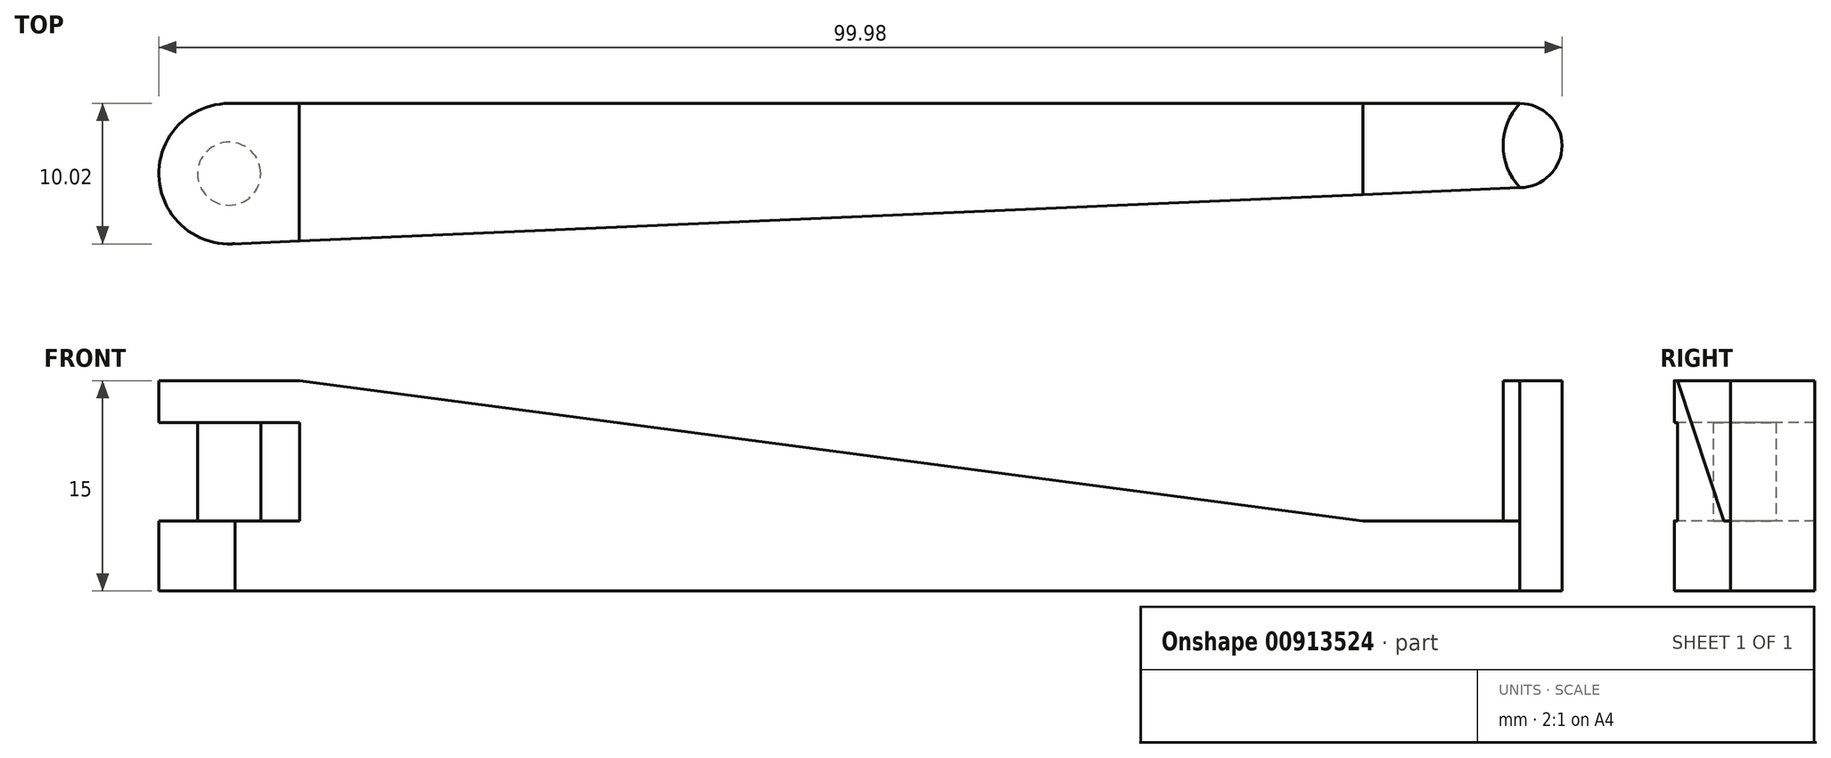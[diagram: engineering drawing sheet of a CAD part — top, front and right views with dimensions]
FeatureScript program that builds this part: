
annotation { "Feature Type Name" : "Feature", "Feature Type Description" : "" }
export const myFeature = defineFeature(function(context is Context, id is Id, definition is map)
    precondition{}
    {
        {
            var Q0;
            Q0=qCreatedBy(makeId("Top.planeOp"),FACE);
            var sketch = newSketch(context, id + "F0", { "sketchPlane" : qUnion([Q0])});
            skArc(sketch, "E0", {"start": v(0, -21.01) * mm, "mid": v(-5, -26.24) * mm, "end": v(0.44, -31.01) * mm});
            skLineSegment(sketch, "E1", {"start": v(0, -21.01) * mm, "end": v(91.97, -21.01) * mm});
            skArc(sketch, "E2", {"start": v(91.97, -27.01) * mm, "mid": v(94.97, -24.01) * mm, "end": v(91.97, -21.01) * mm});
            skLineSegment(sketch, "E3", {"start": v(0, -31.03) * mm, "end": v(91.97, -27.01) * mm});
            skSolve(sketch);
        }
        {
            var Q0;
            Q0 = qSketchRegion(id + "F0", true);
            extrude(context, id + "F1", {"entities" : qUnion([Q0]), "depth" : 5 * mm, "offsetDistance" : 25 * mm});
        }
        {
            var Q0;
            Q0=makeQuery(id+"F1.opExtrude","CAP_FACE",FACE,{"disambiguationData":[OSD([sQuery(id+"F0.wireOp",EDGE,"E0"),sQuery(id+"F0.wireOp",EDGE,"E1"),sQuery(id+"F0.wireOp",EDGE,"E2"),sQuery(id+"F0.wireOp",EDGE,"E3")])],"isStart":false});
            var sketch = newSketch(context, id + "F2", { "sketchPlane" : qUnion([Q0])});
            skArc(sketch, "E4.0", {"start": v(91.97, -27.01) * mm, "mid": v(94.97, -24.01) * mm, "end": v(91.97, -21.01) * mm});
            skPoint(sketch, "E4.1", {"position": v(94.97, -24.01) * mm});
            skArc(sketch, "E5", {"start": v(91.97, -21.01) * mm, "mid": v(90.77, -24.01) * mm, "end": v(91.97, -27.01) * mm});
            skSolve(sketch);
        }
        {
            var Q0;
            Q0 = qSketchRegion(id + "F2", true);
            extrude(context, id + "F3", {"entities" : qUnion([Q0]), "operationType" : NewBodyOperationType.ADD, "depth" : 10 * mm, "offsetDistance" : 25 * mm});
        }
        {
            var Q0;
            Q0=makeQuery(id+"F1.opExtrude","CAP_FACE",FACE,{"disambiguationData":[OSD([sQuery(id+"F0.wireOp",EDGE,"E0"),sQuery(id+"F0.wireOp",EDGE,"E1"),sQuery(id+"F0.wireOp",EDGE,"E2"),sQuery(id+"F0.wireOp",EDGE,"E3")])],"isStart":false});
            var sketch = newSketch(context, id + "F4", { "sketchPlane" : qUnion([Q0])});
            skCircle(sketch, "E6", {"center": v(0, -26.02) * mm, "radius": 2.25 * mm});
            skCircle(sketch, "E7", {"center": v(0, -26.02) * mm, "radius": 5 * mm});
            skSolve(sketch);
        }
        {
            var Q0;
            Q0=makeQuery(id+"F4.imprint","IMPRINT",FACE,{"disambiguationData":[TD([[makeQuery(id+"F4.imprint","IMPRINT",EDGE,{"derivedFrom":sQuery(id+"F4.wireOp",EDGE,"E6")}),1.0]])]});
            extrude(context, id + "F5", {"entities" : qUnion([Q0]), "operationType" : NewBodyOperationType.ADD, "depth" : 10 * mm, "offsetDistance" : 25 * mm});
        }
        {
            var Q0;
            {var subQ1=makeQuery(id+"F1.opExtrude","CAP_EDGE",EDGE,{"disambiguationData":[OSD([sQuery(id+"F0.wireOp",EDGE,"E1")])],"isStart":false});Q0=makeQuery(id+"F4.imprint","IMPRINT",FACE,{"disambiguationData":[TD([[makeQuery(id+"F4.imprint","IMPRINT",EDGE,{"derivedFrom":subQ1}),-1.0]])]});}
            var sketch = newSketch(context, id + "F6", { "sketchPlane" : qUnion([Q0])});
            skArc(sketch, "E8.0", {"start": v(0.44, -31.01) * mm, "mid": v(5, -25.8) * mm, "end": v(0, -21.01) * mm});
            skLineSegment(sketch, "E8.1", {"start": v(0, -21.01) * mm, "end": v(80.77, -21.01) * mm});
            skLineSegment(sketch, "E8.2", {"start": v(0.44, -31.01) * mm, "end": v(80.77, -27.5) * mm});
            skLineSegment(sketch, "E9", {"start": v(80.77, -21.01) * mm, "end": v(80.77, -27.5) * mm});
            skPoint(sketch, "E10.orphan", {"position": v(91.97, -27.01) * mm});
            skPoint(sketch, "E11.orphan", {"position": v(91.97, -21.01) * mm});
            skLineSegment(sketch, "E12", {"start": v(5, -21.01) * mm, "end": v(5, -30.81) * mm});
            skSolve(sketch);
        }
        {
            var Q0;
            {var subQ4=sQuery(id+"F6.wireOp",EDGE,"E9");Q0=makeQuery(id+"F6.imprint","IMPRINT",FACE,{"disambiguationData":[TD([[makeQuery(id+"F6.imprint","IMPRINT",EDGE,{"derivedFrom":subQ4}),-1.0]])]});}
            extrude(context, id + "F7", {"entities" : qUnion([Q0]), "operationType" : NewBodyOperationType.ADD, "depth" : 10 * mm, "offsetDistance" : 25 * mm});
        }
        {
            var Q0;
            Q0=makeQuery(id+"F5.opExtrude","CAP_FACE",FACE,{"disambiguationData":[OSD([sQuery(id+"F4.wireOp",EDGE,"E6")])],"isStart":false});
            var sketch = newSketch(context, id + "F8", { "sketchPlane" : qUnion([Q0])});
            skArc(sketch, "E13", {"start": v(0, -21.01) * mm, "mid": v(-5, -26.14) * mm, "end": v(0.22, -31.03) * mm});
            skLineSegment(sketch, "E14.0", {"start": v(5, -21.01) * mm, "end": v(5, -30.81) * mm});
            skLineSegment(sketch, "E15", {"start": v(0, -21.01) * mm, "end": v(5, -21.01) * mm});
            skLineSegment(sketch, "E16", {"start": v(5, -30.81) * mm, "end": v(0, -31.04) * mm});
            skSolve(sketch);
        }
        {
            var Q0;
            Q0 = qSketchRegion(id + "F8", true);
            extrude(context, id + "F9", {"entities" : qUnion([Q0]), "operationType" : NewBodyOperationType.ADD, "oppositeDirection" : true, "depth" : 3 * mm, "offsetDistance" : 25 * mm});
        }
        {
            var Q0;
            Q0=makeQuery(id+"F7.boolean.opBoolean","MERGE",FACE,{"derivedFrom":[makeQuery(id+"F1.opExtrude","SWEPT_FACE",FACE,{"disambiguationData":[OSD([sQuery(id+"F0.wireOp",EDGE,"E1")])]}),makeQuery(id+"F7.opExtrude","SWEPT_FACE",FACE,{"disambiguationData":[OSD([sQuery(id+"F6.wireOp",EDGE,"E8.1")])]})]});
            var sketch = newSketch(context, id + "F10", { "sketchPlane" : qUnion([Q0])});
            skLineSegment(sketch, "E17", {"start": v(-80.77, 5) * mm, "end": v(-5, 15) * mm});
            skLineSegment(sketch, "E18", {"start": v(0, 15) * mm, "end": v(-5, 15) * mm});
            skLineSegment(sketch, "E19", {"start": v(-5, 15) * mm, "end": v(-80.77, 15) * mm});
            skLineSegment(sketch, "E20", {"start": v(-80.77, 15) * mm, "end": v(-80.77, 5) * mm});
            skSolve(sketch);
        }
        {
            var Q0;
            Q0 = qSketchRegion(id + "F10", true);
            extrude(context, id + "F11", {"entities" : qUnion([Q0]), "operationType" : NewBodyOperationType.REMOVE, "oppositeDirection" : true, "depth" : 25 * mm, "offsetDistance" : 25 * mm});
        }
    });
